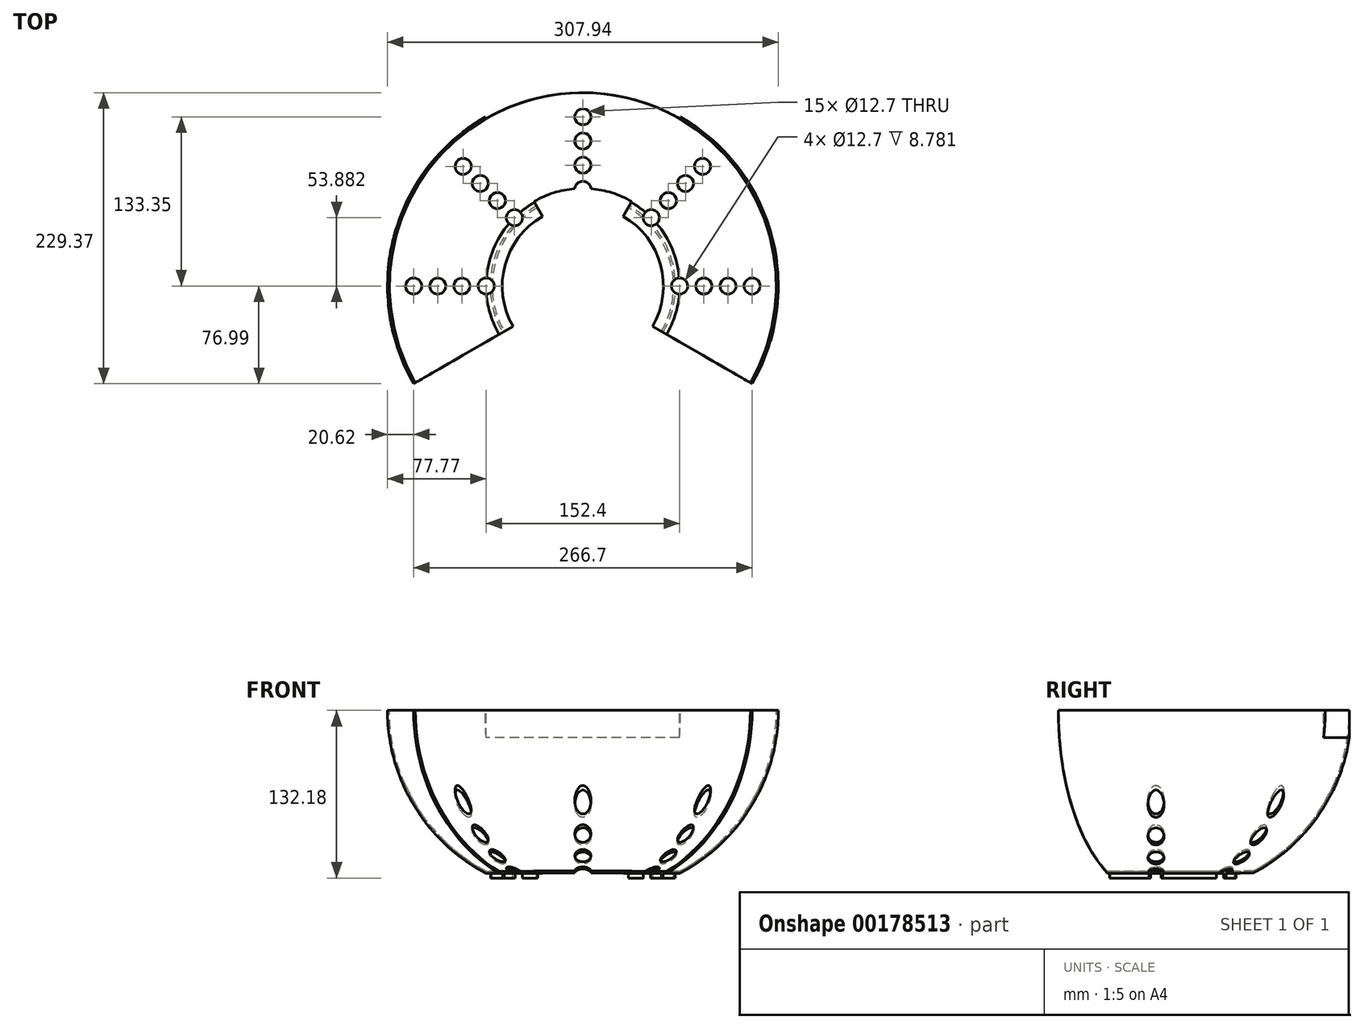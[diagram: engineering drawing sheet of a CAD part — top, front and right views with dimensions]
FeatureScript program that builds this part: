
annotation { "Feature Type Name" : "Feature", "Feature Type Description" : "" }
export const myFeature = defineFeature(function(context is Context, id is Id, definition is map)
    precondition{}
    {
        {
            var Q0;
            Q0=qCreatedBy(makeId("Front.planeOp"),FACE);
            var sketch = newSketch(context, id + "F0", { "sketchPlane" : qUnion([Q0])});
            skLineSegment(sketch, "E0", {"start": v(0, 1.59) * mm, "end": v(-76.2, 1.59) * mm});
            skLineSegment(sketch, "E1", {"start": v(0, 1.59) * mm, "end": v(0, 0) * mm});
            skLineSegment(sketch, "E2", {"start": v(-73.03, 0) * mm, "end": v(-73.03, -3.6) * mm});
            skLineSegment(sketch, "E3", {"start": v(-73.03, -3.6) * mm, "end": v(-71.44, -3.6) * mm});
            skLineSegment(sketch, "E4", {"start": v(-71.44, -3.6) * mm, "end": v(-71.44, 0) * mm});
            skArc(sketch, "E5", {"start": v(-152.38, 128.59) * mm, "mid": v(-131.88, 54.54) * mm, "end": v(-76.2, 1.59) * mm});
            skLineSegment(sketch, "E6", {"start": v(-152.38, 128.59) * mm, "end": v(-153.97, 128.59) * mm});
            skArc(sketch, "E7", {"start": v(-153.97, 128.59) * mm, "mid": v(-133.02, 53.45) * mm, "end": v(-76.2, 0) * mm});
            skLineSegment(sketch, "E8", {"start": v(-76.2, 0) * mm, "end": v(-73.03, 0) * mm});
            skLineSegment(sketch, "E9", {"start": v(-71.44, 0) * mm, "end": v(0, 0) * mm});
            skSolve(sketch);
        }
        {
            var Q0;
            Q0 = qSketchRegion(id + "F0", true);
            var Q1;
            Q1 = qConstructionFilter(qBodyType(qCreatedBy(id + "F0" ,EDGE), BodyType.WIRE), ConstructionObject.NO);
            var Q2;
            Q2=sQuery(id+"F0.wireOp",EDGE,"E1");
            revolve(context, id + "F1", {"entities" : qUnion([Q0]), "surfaceEntities" : qUnion([Q1]), "axis" : qUnion([Q2]), "revolveType" : RevolveType.FULL});
        }
        {
            var Q0;
            Q0=makeQuery(id+"F1.opRevolve","SWEPT_FACE",FACE,{"disambiguationData":[OSD([sQuery(id+"F0.wireOp",EDGE,"E6")])]});
            var sketch = newSketch(context, id + "F2", { "sketchPlane" : qUnion([Q0])});
            skLineSegment(sketch, "E10", {"start": v(0, 0) * mm, "end": v(-133.34, -76.99) * mm});
            skLineSegment(sketch, "E11", {"start": v(0, 0) * mm, "end": v(133.34, -76.99) * mm});
            skLineSegment(sketch, "E12", {"start": v(0, 0) * mm, "end": v(-76.99, 133.34) * mm});
            skLineSegment(sketch, "E13", {"start": v(-76.99, 133.34) * mm, "end": v(0, 0) * mm});
            skLineSegment(sketch, "E14", {"start": v(0, 0) * mm, "end": v(76.99, 133.34) * mm});
            skArc(sketch, "E15", {"start": v(-133.34, -76.99) * mm, "mid": v(0, -153.97) * mm, "end": v(133.34, -76.99) * mm});
            skArc(sketch, "E16", {"start": v(-76.99, 133.34) * mm, "mid": v(0, 153.97) * mm, "end": v(76.99, 133.34) * mm});
            skArc(sketch, "E17", {"start": v(-38.5, 66.67) * mm, "mid": v(0, 76.99) * mm, "end": v(38.5, 66.67) * mm});
            skCircle(sketch, "E18", {"center": v(0, 0) * mm, "radius": 63.5 * mm});
            skSolve(sketch);
        }
        {
            var Q0;
            {var subQ0=sQuery(id+"F2.wireOp",EDGE,"E17");Q0=makeQuery(id+"F2.imprint","IMPRINT",FACE,{"disambiguationData":[TD([[makeQuery(id+"F2.imprint","IMPRINT",EDGE,{"derivedFrom":subQ0}),1.0]])]});}
            var Q1;
            {var subQ1=sQuery(id+"F2.wireOp",EDGE,"E10");var subQ3=makeQuery(id+"F1.opRevolve","SWEPT_EDGE",EDGE,{"disambiguationData":[OSD([sQuery(id+"F0.wireOp",EDGE,"E5"),sQuery(id+"F0.wireOp",EDGE,"E6")])]});var subQ4=makeQuery(id+"F2.imprint","INTERSECT",VERTEX,{"derivedFrom":[subQ3,subQ1]});Q1=makeQuery(id+"F2.imprint","IMPRINT",FACE,{"disambiguationData":[TD([[makeQuery(id+"F2.imprint","IMPRINT",EDGE,{"disambiguationData":[TD([[subQ4,1.0]])],"derivedFrom":subQ1}),1.0]])]});}
            var Q2;
            {var subQ0=sQuery(id+"F2.wireOp",EDGE,"E16");Q2=makeQuery(id+"F2.imprint","IMPRINT",FACE,{"disambiguationData":[TD([[makeQuery(id+"F2.imprint","IMPRINT",EDGE,{"derivedFrom":subQ0}),1.0]])]});}
            var Q3;
            {var subQ0=sQuery(id+"F2.wireOp",EDGE,"E15");Q3=makeQuery(id+"F2.imprint","IMPRINT",FACE,{"disambiguationData":[TD([[makeQuery(id+"F2.imprint","IMPRINT",EDGE,{"derivedFrom":subQ0}),1.0]])]});}
            var Q4;
            {var subQ1=sQuery(id+"F2.wireOp",EDGE,"E10");var subQ3=sQuery(id+"F2.wireOp",EDGE,"E18");var subQ4=makeQuery(id+"F2.imprint","INTERSECT",VERTEX,{"derivedFrom":[subQ1,subQ3]});Q4=makeQuery(id+"F2.imprint","IMPRINT",FACE,{"disambiguationData":[TD([[makeQuery(id+"F2.imprint","IMPRINT",EDGE,{"disambiguationData":[TD([[subQ4,1.0]])],"derivedFrom":subQ3}),1.0]])]});}
            var Q5;
            {var subQ1=sQuery(id+"F2.wireOp",EDGE,"E10");var subQ3=sQuery(id+"F2.wireOp",EDGE,"E18");var subQ4=makeQuery(id+"F2.imprint","INTERSECT",VERTEX,{"derivedFrom":[subQ1,subQ3]});Q5=makeQuery(id+"F2.imprint","IMPRINT",FACE,{"disambiguationData":[TD([[makeQuery(id+"F2.imprint","IMPRINT",EDGE,{"disambiguationData":[TD([[subQ4,-1.0]])],"derivedFrom":subQ3}),1.0]])]});}
            var Q6;
            {var subQ1=sQuery(id+"F2.wireOp",EDGE,"E11");var subQ3=sQuery(id+"F2.wireOp",EDGE,"E18");var subQ4=makeQuery(id+"F2.imprint","INTERSECT",VERTEX,{"derivedFrom":[subQ1,subQ3]});Q6=makeQuery(id+"F2.imprint","IMPRINT",FACE,{"disambiguationData":[TD([[makeQuery(id+"F2.imprint","IMPRINT",EDGE,{"disambiguationData":[TD([[subQ4,-1.0]])],"derivedFrom":subQ3}),1.0]])]});}
            var Q7;
            {var subQ1=sQuery(id+"F2.wireOp",EDGE,"E13");var subQ3=sQuery(id+"F2.wireOp",EDGE,"E18");var subQ4=makeQuery(id+"F2.imprint","INTERSECT",VERTEX,{"derivedFrom":[subQ1,subQ3]});Q7=makeQuery(id+"F2.imprint","IMPRINT",FACE,{"disambiguationData":[TD([[makeQuery(id+"F2.imprint","IMPRINT",EDGE,{"disambiguationData":[TD([[subQ4,1.0]])],"derivedFrom":subQ3}),1.0]])]});}
            extrude(context, id + "F3", {"entities" : qUnion([Q0, Q1, Q2, Q3, Q4, Q5, Q6, Q7]), "operationType" : NewBodyOperationType.REMOVE, "oppositeDirection" : true, "depth" : 177.8 * mm});
        }
        {
            var Q0;
            Q0=makeQuery(id+"F3.boolean.opBoolean","SPLIT",FACE,{"disambiguationData":[TD([makeQuery(id+"F3.opExtrude","SWEPT_FACE",FACE,{"disambiguationData":[OSD([sQuery(id+"F2.wireOp",EDGE,"E10")])]})])],"derivedFrom":makeQuery(id+"F1.opRevolve","SWEPT_FACE",FACE,{"disambiguationData":[OSD([sQuery(id+"F0.wireOp",EDGE,"E6")])]})});
            var sketch = newSketch(context, id + "F4", { "sketchPlane" : qUnion([Q0])});
            skCircle(sketch, "E19", {"center": v(0, 0) * mm, "radius": 6.35 * mm});
            skCircle(sketch, "E20.1.0.0", {"center": v(19.05, 0) * mm, "radius": 6.35 * mm});
            skCircle(sketch, "E20.2.0.0", {"center": v(38.1, 0) * mm, "radius": 6.35 * mm});
            skCircle(sketch, "E20.3.0.0", {"center": v(57.15, 0) * mm, "radius": 6.35 * mm});
            skCircle(sketch, "E20.4.0.0", {"center": v(76.2, 0) * mm, "radius": 6.35 * mm});
            skCircle(sketch, "E20.5.0.0", {"center": v(95.25, 0) * mm, "radius": 6.35 * mm});
            skCircle(sketch, "E20.6.0.0", {"center": v(114.3, 0) * mm, "radius": 6.35 * mm});
            skCircle(sketch, "E20.7.0.0", {"center": v(133.35, 0) * mm, "radius": 6.35 * mm});
            skLineSegment(sketch, "E20.direction1", {"start": v(0, 0) * mm, "end": v(19.05, 0) * mm, "construction": true});
            skCircle(sketch, "E21.1.1", {"center": v(13.47, 13.47) * mm, "radius": 6.35 * mm});
            skCircle(sketch, "E21.1.2", {"center": v(26.94, 26.94) * mm, "radius": 6.35 * mm});
            skCircle(sketch, "E21.1.3", {"center": v(40.41, 40.41) * mm, "radius": 6.35 * mm});
            skCircle(sketch, "E21.1.4", {"center": v(53.88, 53.88) * mm, "radius": 6.35 * mm});
            skCircle(sketch, "E21.1.5", {"center": v(67.35, 67.35) * mm, "radius": 6.35 * mm});
            skCircle(sketch, "E21.1.6", {"center": v(80.82, 80.82) * mm, "radius": 6.35 * mm});
            skCircle(sketch, "E21.1.7", {"center": v(94.3, 94.3) * mm, "radius": 6.35 * mm});
            skCircle(sketch, "E21.2.1", {"center": v(0, 19.05) * mm, "radius": 6.35 * mm});
            skCircle(sketch, "E21.2.2", {"center": v(0, 38.1) * mm, "radius": 6.35 * mm});
            skCircle(sketch, "E21.2.3", {"center": v(0, 57.15) * mm, "radius": 6.35 * mm});
            skCircle(sketch, "E21.2.4", {"center": v(0, 76.2) * mm, "radius": 6.35 * mm});
            skCircle(sketch, "E21.2.5", {"center": v(0, 95.25) * mm, "radius": 6.35 * mm});
            skCircle(sketch, "E21.2.6", {"center": v(0, 114.3) * mm, "radius": 6.35 * mm});
            skCircle(sketch, "E21.2.7", {"center": v(0, 133.35) * mm, "radius": 6.35 * mm});
            skCircle(sketch, "E21.3.1", {"center": v(-13.47, 13.47) * mm, "radius": 6.35 * mm});
            skCircle(sketch, "E21.3.2", {"center": v(-26.94, 26.94) * mm, "radius": 6.35 * mm});
            skCircle(sketch, "E21.3.3", {"center": v(-40.41, 40.41) * mm, "radius": 6.35 * mm});
            skCircle(sketch, "E21.3.4", {"center": v(-53.88, 53.88) * mm, "radius": 6.35 * mm});
            skCircle(sketch, "E21.3.5", {"center": v(-67.35, 67.35) * mm, "radius": 6.35 * mm});
            skCircle(sketch, "E21.3.6", {"center": v(-80.82, 80.82) * mm, "radius": 6.35 * mm});
            skCircle(sketch, "E21.3.7", {"center": v(-94.3, 94.3) * mm, "radius": 6.35 * mm});
            skCircle(sketch, "E22.2.4.0", {"center": v(-19.05, 0) * mm, "radius": 6.35 * mm});
            skCircle(sketch, "E22.4.4.0", {"center": v(-38.1, 0) * mm, "radius": 6.35 * mm});
            skCircle(sketch, "E22.6.4.0", {"center": v(-57.15, 0) * mm, "radius": 6.35 * mm});
            skCircle(sketch, "E22.8.4.0", {"center": v(-76.2, 0) * mm, "radius": 6.35 * mm});
            skCircle(sketch, "E22.10.4.0", {"center": v(-95.25, 0) * mm, "radius": 6.35 * mm});
            skCircle(sketch, "E22.12.4.0", {"center": v(-114.3, 0) * mm, "radius": 6.35 * mm});
            skCircle(sketch, "E22.14.4.0", {"center": v(-133.35, 0) * mm, "radius": 6.35 * mm});
            skCircle(sketch, "E22.2.5.0", {"center": v(-13.47, -13.47) * mm, "radius": 6.35 * mm});
            skCircle(sketch, "E22.4.5.0", {"center": v(-26.94, -26.94) * mm, "radius": 6.35 * mm});
            skCircle(sketch, "E22.6.5.0", {"center": v(-40.41, -40.41) * mm, "radius": 6.35 * mm});
            skCircle(sketch, "E22.8.5.0", {"center": v(-53.88, -53.88) * mm, "radius": 6.35 * mm});
            skCircle(sketch, "E22.10.5.0", {"center": v(-67.35, -67.35) * mm, "radius": 6.35 * mm});
            skCircle(sketch, "E22.12.5.0", {"center": v(-80.82, -80.82) * mm, "radius": 6.35 * mm});
            skCircle(sketch, "E22.14.5.0", {"center": v(-94.3, -94.3) * mm, "radius": 6.35 * mm});
            skCircle(sketch, "E22.2.6.0", {"center": v(0, -19.05) * mm, "radius": 6.35 * mm});
            skCircle(sketch, "E22.4.6.0", {"center": v(0, -38.1) * mm, "radius": 6.35 * mm});
            skCircle(sketch, "E22.6.6.0", {"center": v(0, -57.15) * mm, "radius": 6.35 * mm});
            skCircle(sketch, "E22.8.6.0", {"center": v(0, -76.2) * mm, "radius": 6.35 * mm});
            skCircle(sketch, "E22.10.6.0", {"center": v(0, -95.25) * mm, "radius": 6.35 * mm});
            skCircle(sketch, "E22.12.6.0", {"center": v(0, -114.3) * mm, "radius": 6.35 * mm});
            skCircle(sketch, "E22.14.6.0", {"center": v(0, -133.35) * mm, "radius": 6.35 * mm});
            skCircle(sketch, "E22.2.7.0", {"center": v(13.47, -13.47) * mm, "radius": 6.35 * mm});
            skCircle(sketch, "E22.4.7.0", {"center": v(26.94, -26.94) * mm, "radius": 6.35 * mm});
            skCircle(sketch, "E22.6.7.0", {"center": v(40.41, -40.41) * mm, "radius": 6.35 * mm});
            skCircle(sketch, "E22.8.7.0", {"center": v(53.88, -53.88) * mm, "radius": 6.35 * mm});
            skCircle(sketch, "E22.10.7.0", {"center": v(67.35, -67.35) * mm, "radius": 6.35 * mm});
            skCircle(sketch, "E22.12.7.0", {"center": v(80.82, -80.82) * mm, "radius": 6.35 * mm});
            skCircle(sketch, "E22.14.7.0", {"center": v(94.3, -94.3) * mm, "radius": 6.35 * mm});
            skSolve(sketch);
        }
        {
            var Q0;
            Q0 = qSketchRegion(id + "F4", true);
            extrude(context, id + "F5", {"entities" : qUnion([Q0]), "operationType" : NewBodyOperationType.REMOVE, "oppositeDirection" : true, "depth" : 177.8 * mm});
        }
    });
